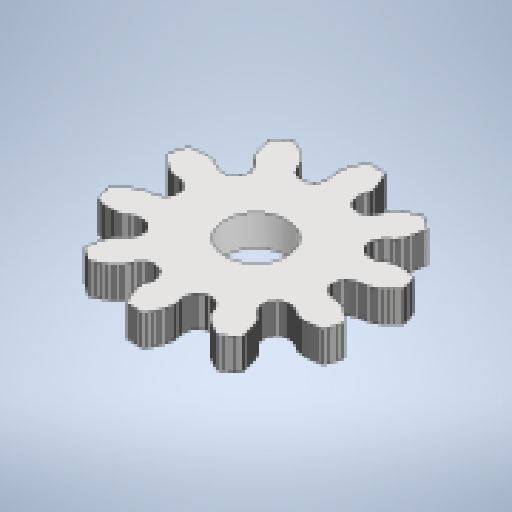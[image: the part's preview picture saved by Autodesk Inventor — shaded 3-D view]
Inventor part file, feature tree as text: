
AUTODESK INVENTOR PART (.ipt)
format: ipt  version: 2024 (Build 280153000, 153)  size: 2,084,352 bytes
history: native  units: mm
features: extrude x3, other x2, sketch x2
ambient origin geometry x8: Origin, YZ Plane, XZ Plane, XY Plane, X Axis, Y Axis, Z Axis, Center Point
bodies: Body1 (feature_tree)
feature tree (7):
  other  "作業平面1"
  sketch  "スケッチ5"
  extrude  "押し出し5"  Depth=3.5mm
  extrude  "押し出し6"  TaperAngle=0.0deg  [1 undecoded]
  extrude  "押し出し4"  Depth=130.0mm TaperAngle=360.0deg
  sketch  "スケッチ4"
  other  "ソリッド3"
note: 1 required parameter value undecoded (feature->parameter linkage not recoverable at this tier; creation-order binding heuristic only, values carry confidence <= 0.55)
